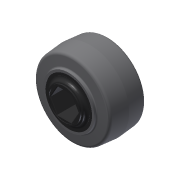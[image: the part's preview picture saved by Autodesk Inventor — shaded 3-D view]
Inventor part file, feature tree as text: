
AUTODESK INVENTOR PART (.ipt)
format: ipt  version: 2015 (Build 190159000, 159)  size: 295,936 bytes
history: native  units: in
note: dims shown in document units (in); Inventor stores cm internally (conversion verified against a paired STEP export)
features: boolean_combine x1, other x1, extrude x1, mirror x1, imported_body x1, sketch x1
ambient origin geometry x8: Origin, YZ Plane, XZ Plane, XY Plane, X Axis, Y Axis, Z Axis, Center Point
bodies: Body1 (feature_tree)
feature tree (6):
  boolean_combine  "Combine2"
  other  "217-4045-STEP-201410151"
  extrude  "Extrusion1"  Depth=0.0039in TaperAngle=0.0deg
  mirror  "Mirror1"
  imported_body  "Base1"
  sketch  "Sketch1"  dims[d0=0.9646in d1=0.0039in d2=0.0in]
